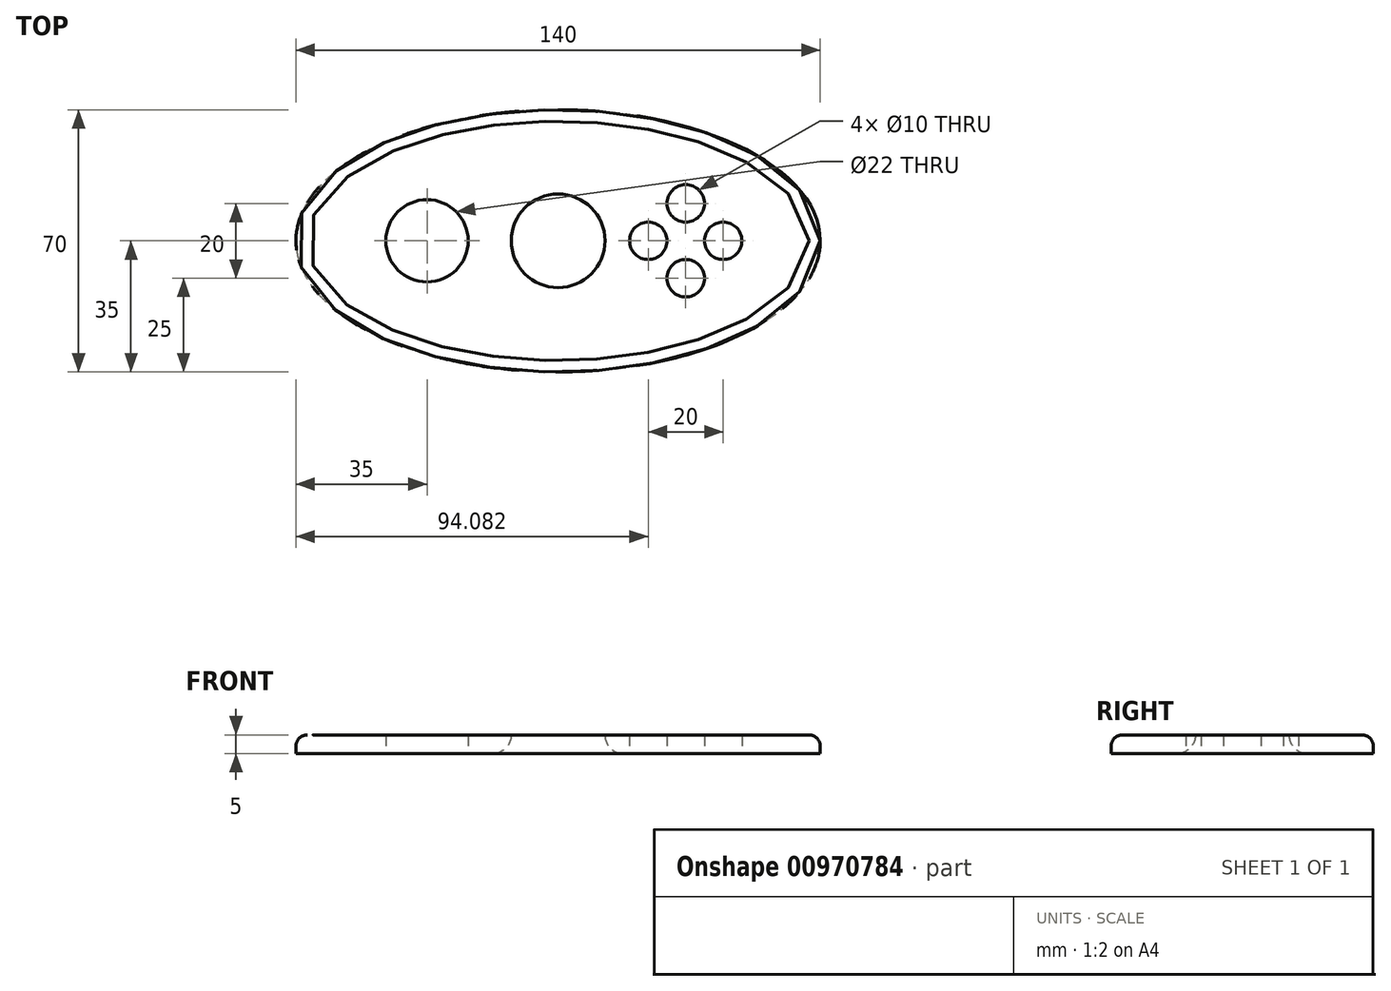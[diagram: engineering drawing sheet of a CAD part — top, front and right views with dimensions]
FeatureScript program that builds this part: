
annotation { "Feature Type Name" : "Feature", "Feature Type Description" : "" }
export const myFeature = defineFeature(function(context is Context, id is Id, definition is map)
    precondition{}
    {
        {
            var Q0;
            Q0=qCreatedBy(makeId("Top.planeOp"),FACE);
            var sketch = newSketch(context, id + "F0", { "sketchPlane" : qUnion([Q0])});
            skPoint(sketch, "E0.middle", {"position": v(0, 0) * mm});
            skPoint(sketch, "E0.top.start.orphan", {"position": v(147.55, -98.37) * mm});
            skPoint(sketch, "E0.right.end.orphan", {"position": v(-147.55, -98.37) * mm});
            skPoint(sketch, "E0.bottom.end.orphan", {"position": v(-147.55, 98.37) * mm});
            skPoint(sketch, "E0.bottom.start.orphan", {"position": v(147.55, 98.37) * mm});
            skEllipse(sketch, "E1", {"center": v(0, 0) * mm, "majorRadius": 70 * mm, "minorRadius": 35 * mm, "majorAxis": v(1, 0)});
            skCircle(sketch, "E2", {"center": v(0, 0) * mm, "radius": 12.5 * mm});
            skPoint(sketch, "E3.middle", {"position": v(-35, 0) * mm});
            skPoint(sketch, "E4.end.orphan", {"position": v(-45, 0) * mm});
            skPoint(sketch, "E4.start.orphan", {"position": v(-38.75, 0) * mm});
            skPoint(sketch, "E5.orphan", {"position": v(-25, 0) * mm});
            skPoint(sketch, "E6.orphan", {"position": v(-38.75, -3.75) * mm});
            skPoint(sketch, "E3.bottom.start.orphan", {"position": v(-31.25, -3.75) * mm});
            skPoint(sketch, "E7.start.orphan", {"position": v(-0.92, 0) * mm});
            skCircle(sketch, "E8", {"center": v(24.08, 0) * mm, "radius": 5 * mm});
            skCircle(sketch, "E9", {"center": v(34.08, -10) * mm, "radius": 5 * mm});
            skCircle(sketch, "E10", {"center": v(44.08, 0) * mm, "radius": 5 * mm});
            skCircle(sketch, "E11", {"center": v(34.08, 10) * mm, "radius": 5 * mm});
            skCircle(sketch, "E12", {"center": v(-35, 0) * mm, "radius": 11 * mm});
            skPoint(sketch, "E13.orphan", {"position": v(-45, -3.75) * mm});
            skPoint(sketch, "E14.start.orphan", {"position": v(-31.25, 3.75) * mm});
            skPoint(sketch, "E15.start.orphan", {"position": v(-38.75, 3.75) * mm});
            skSolve(sketch);
        }
        {
            var Q0;
            Q0 = qSketchRegion(id + "F0", true);
            extrude(context, id + "F1", {"entities" : qUnion([Q0]), "depth" : 5 * mm, "offsetDistance" : 25 * mm});
        }
        {
            var Q0;
            Q0=makeQuery(id+"F1.opExtrude","CAP_EDGE",EDGE,{"disambiguationData":[OSD([sQuery(id+"F0.wireOp",EDGE,"E2")])],"isStart":true});
            fillet(context, id + "F2", {"entities" : qUnion([Q0]), "radius" : 5 * mm, "tangentPropagation" : true, "allowEdgeOverflow" : false});
        }
        {
            var Q0;
            Q0=makeQuery(id+"F1.opExtrude","CAP_EDGE",EDGE,{"disambiguationData":[OSD([sQuery(id+"F0.wireOp",EDGE,"E1")])],"isStart":false});
            fillet(context, id + "F3", {"entities" : qUnion([Q0]), "radius" : 3 * mm, "tangentPropagation" : true, "allowEdgeOverflow" : false});
        }
    });
